# Revit family: ENCP450J
name_source: partatom
category: HLS-Bauteile
revit_build: Autodesk Revit 2016 (Build: 20150714_1515(x64)
units: mm (PartAtom-declared; Revit-internal decimal feet)

## family parameters
Arbeitsebenenbasiert = Nein
Beim Laden mit Abzugskörper schneiden = Nein
Bemaßung runder Anschluss = Durchmesser verwenden
Gemeinsam genutzt = Nein
Immer vertikal = Ja
OmniClass-Nummer = 23.75.10.21
OmniClass-Titel = Heat Pumps
Raumberechnungspunkt = Nein
Teiletyp = Normal

## types (1)
- ENCP450J
    ALG_Gasversorgungsdruck_in_mbar = 17-25
    ALG_Gewicht_in_kg = 880
    ALG_ManufacturerCode = ENCP450J
    ALG_Schalldruckpegel_Leiselauf_in_dB(A) = 54
    ALG_Schalldruckpegel_Max_in_dB(A) = 62
    ALG_Schalldruckpegel_Nominal_in_dB(A) = 57
    ALG_Ventilator_Externe_Pressung_in_Pa = 5 (30 über Software)
    ALG_Ventilator_Luftmege_in_m3/h = 21600
    Beschreibung = Gasmotorwärmepumpe
    HLS_Bezeichnung_2 = ENCP450J
    HLS_Breite = 800 mm  [stored 2.62467 ft]
    HLS_Höhe = 2170 mm
    HLS_Länge = 1690 mm  [stored 5.54462 ft]
    HLS_Typ = ENCP450J
    Hersteller = YANMAR
    Max Gasaufnahme im VRF Betrieb in kW = 57
    Max Gasaufnahme in Verbindung mit Hydrobox in kW = 69
    Max Gasaufnahme in Verbindung mit RLT-Kit in kW = 57
    Modell = ENCP450J
    Nennleistung im VRF-Betrieb (Heizen) = 50,0
    Nennleistung im VRF-Betrieb (Kühlen) = 45,0
    Nennleistung in Verbindung mit Hydrobox (Heizen) = 46,3
    Nennleistung in Verbindung mit Hydrobox (Kühlen) = 36,3
    Nennleistung in Verbindung mit RLT-Kit (Heizen) = 50,0
    Nennleistung in Verbindung mit RLT-Kit (Kühlen) = 45,0
    Typenkommentare = Gasmotorwärmepumpe
    URL = www.energysystem-yanmar.com

note: [stored X ft] marks values corroborated as IEEE doubles in the binary element streams (Revit-internal decimal feet)

## geometry (parser evidence)
native form markers: Blend x9
no freeform markers — native parametric forms only
